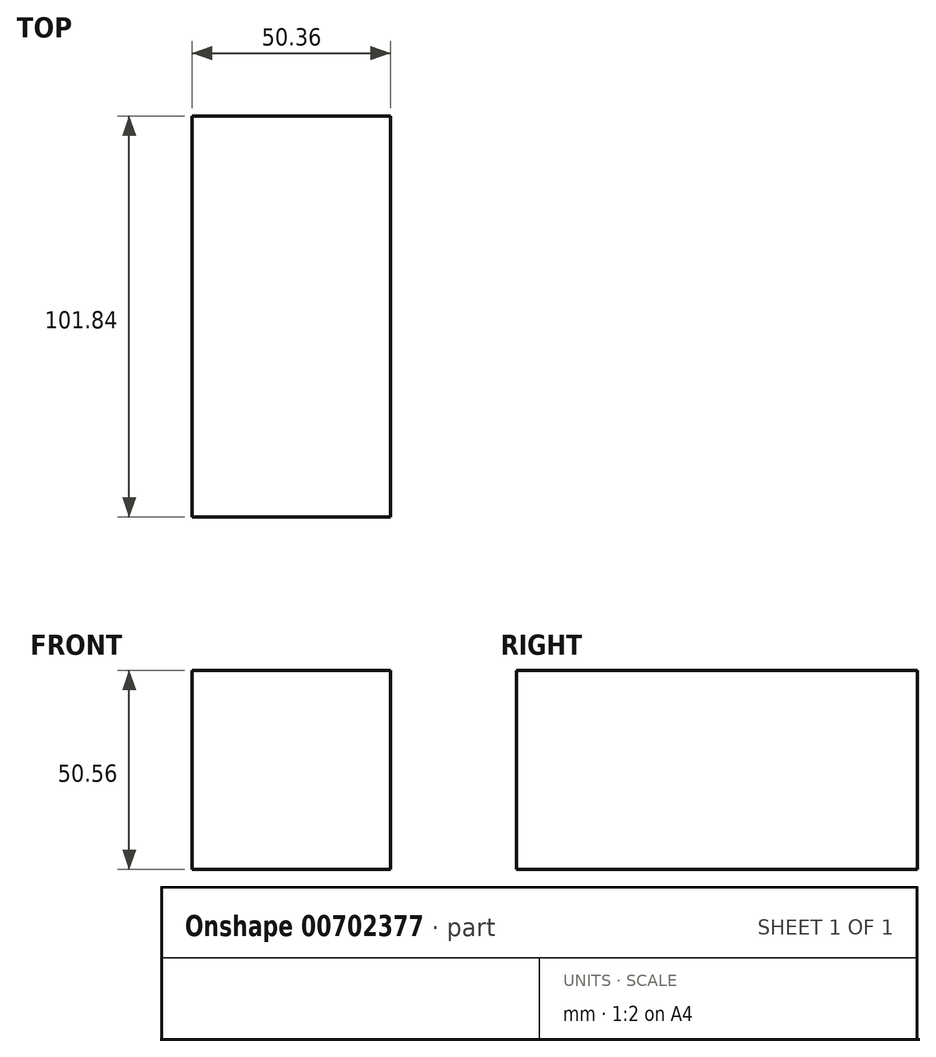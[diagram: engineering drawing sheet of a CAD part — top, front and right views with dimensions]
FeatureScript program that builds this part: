
annotation { "Feature Type Name" : "Feature", "Feature Type Description" : "" }
export const myFeature = defineFeature(function(context is Context, id is Id, definition is map)
    precondition{}
    {
        {
            var Q0;
            Q0=qCreatedBy(makeId("Front.planeOp"),FACE);
            var sketch = newSketch(context, id + "F0", { "sketchPlane" : qUnion([Q0])});
            skLineSegment(sketch, "E0.bottom", {"start": v(0, 0) * mm, "end": v(50.36, 0) * mm});
            skLineSegment(sketch, "E0.top", {"start": v(0, -50.56) * mm, "end": v(50.36, -50.56) * mm});
            skLineSegment(sketch, "E0.left", {"start": v(0, 0) * mm, "end": v(0, -50.56) * mm});
            skLineSegment(sketch, "E0.right", {"start": v(50.36, 0) * mm, "end": v(50.36, -50.56) * mm});
            skSolve(sketch);
        }
        {
            var Q0;
            Q0=makeQuery(id+"F0.imprint","IMPRINT",FACE,{"disambiguationData":[TD([[makeQuery(id+"F0.imprint","IMPRINT",EDGE,{"derivedFrom":sQuery(id+"F0.wireOp",EDGE,"E0.bottom")}),-1.0]])]});
            extrude(context, id + "F1", {"entities" : qUnion([Q0]), "depth" : 101.84 * mm, "offsetDistance" : 25.4 * mm});
        }
    });
